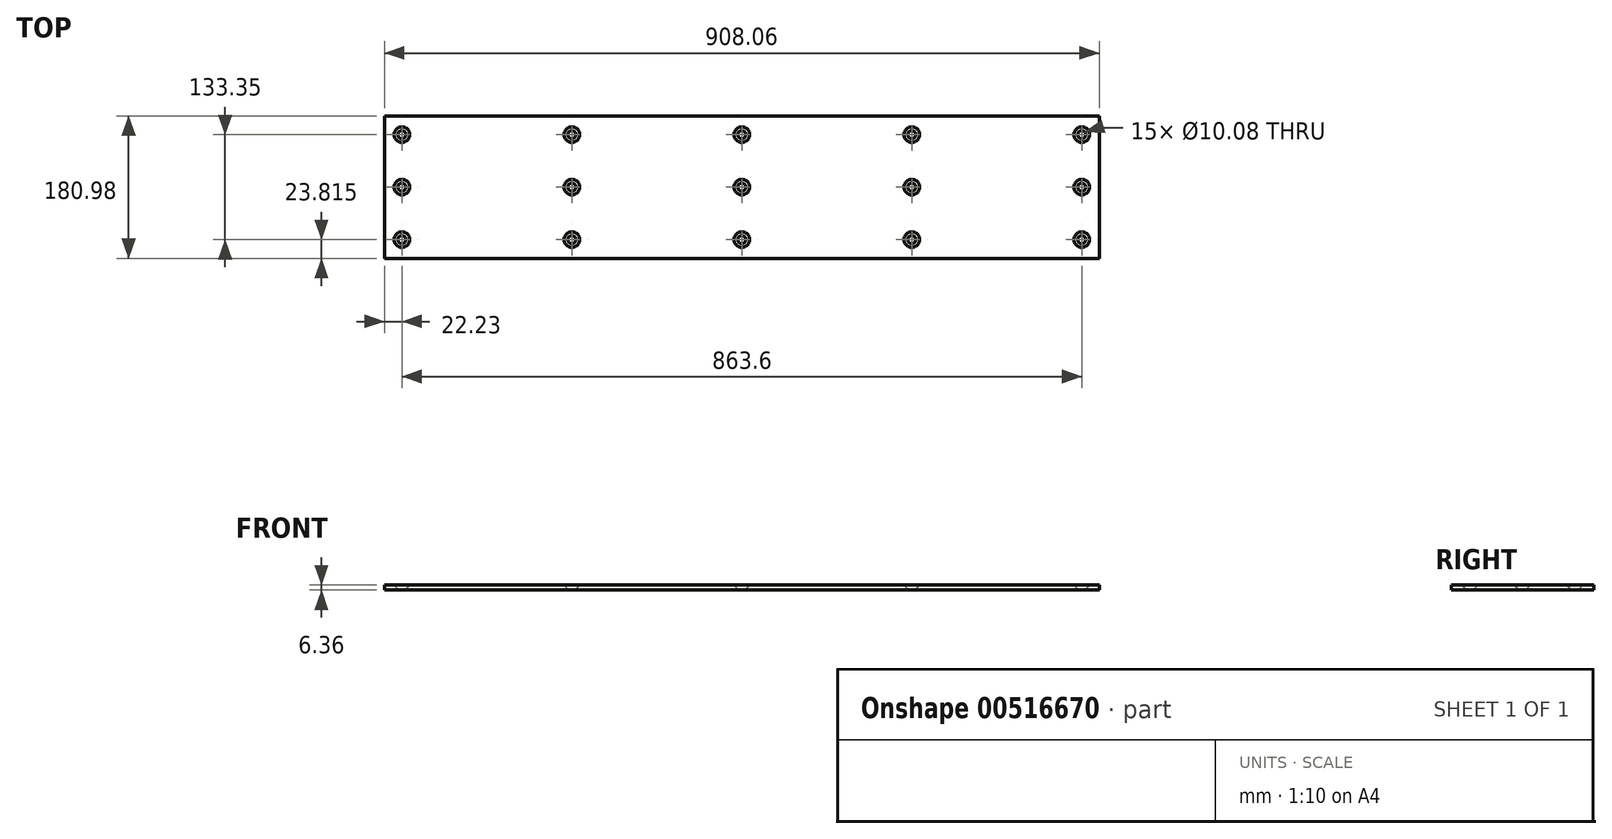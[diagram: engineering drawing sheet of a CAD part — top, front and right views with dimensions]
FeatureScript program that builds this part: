
annotation { "Feature Type Name" : "Feature", "Feature Type Description" : "" }
export const myFeature = defineFeature(function(context is Context, id is Id, definition is map)
    precondition{}
    {
        {
            var Q0;
            Q0=qCreatedBy(makeId("Top.planeOp"),FACE);
            var sketch = newSketch(context, id + "F0", { "sketchPlane" : qUnion([Q0])});
            skLineSegment(sketch, "E0.bottom", {"start": v(454.03, 90.49) * mm, "end": v(-454.03, 90.49) * mm});
            skLineSegment(sketch, "E0.top", {"start": v(454.03, -90.49) * mm, "end": v(-454.03, -90.49) * mm});
            skLineSegment(sketch, "E0.left", {"start": v(454.03, 90.49) * mm, "end": v(454.03, -90.49) * mm});
            skLineSegment(sketch, "E0.right", {"start": v(-454.03, 90.49) * mm, "end": v(-454.03, -90.49) * mm});
            skPoint(sketch, "E0.middle", {"position": v(0, 0) * mm});
            skSolve(sketch);
        }
        {
            var Q0;
            Q0 = qSketchRegion(id + "F0", true);
            extrude(context, id + "F1", {"entities" : qUnion([Q0]), "endBound" : BoundingType.SYMMETRIC, "depth" : 6.35 * mm, "offsetDistance" : 25.4 * mm});
        }
        {
            var Q0;
            Q0=makeQuery(id+"F1.opExtrude","CAP_FACE",FACE,{"disambiguationData":[OSD([sQuery(id+"F0.wireOp",EDGE,"E0.bottom"),sQuery(id+"F0.wireOp",EDGE,"E0.top"),sQuery(id+"F0.wireOp",EDGE,"E0.left"),sQuery(id+"F0.wireOp",EDGE,"E0.right")])],"isStart":false});
            var sketch = newSketch(context, id + "F2", { "sketchPlane" : qUnion([Q0])});
            skPoint(sketch, "E1", {"position": v(-431.8, 66.67) * mm});
            skPoint(sketch, "E2", {"position": v(-431.8, 0) * mm});
            skPoint(sketch, "E3", {"position": v(-431.8, -66.68) * mm});
            skPoint(sketch, "E4", {"position": v(-215.9, -66.68) * mm});
            skPoint(sketch, "E5", {"position": v(-215.9, 0) * mm});
            skPoint(sketch, "E6", {"position": v(-215.9, 66.67) * mm});
            skPoint(sketch, "E7", {"position": v(0, 66.67) * mm});
            skPoint(sketch, "E8", {"position": v(0, 0) * mm});
            skPoint(sketch, "E9", {"position": v(0, -66.68) * mm});
            skPoint(sketch, "E10", {"position": v(215.9, -66.68) * mm});
            skPoint(sketch, "E11", {"position": v(215.9, 0) * mm});
            skPoint(sketch, "E12", {"position": v(215.9, 66.67) * mm});
            skPoint(sketch, "E13", {"position": v(431.8, 66.67) * mm});
            skPoint(sketch, "E14", {"position": v(431.8, -66.68) * mm});
            skPoint(sketch, "E15", {"position": v(431.8, 0) * mm});
            skSolve(sketch);
        }
        {
            var Q0;
            Q0=sQuery(id+"F2.wireOp",VERTEX,"E1");
            var Q1;
            Q1=sQuery(id+"F2.wireOp",VERTEX,"E2");
            var Q2;
            Q2=sQuery(id+"F2.wireOp",VERTEX,"E3");
            var Q3;
            Q3=sQuery(id+"F2.wireOp",VERTEX,"E4");
            var Q4;
            Q4=sQuery(id+"F2.wireOp",VERTEX,"E5");
            var Q5;
            Q5=sQuery(id+"F2.wireOp",VERTEX,"E6");
            var Q6;
            Q6=sQuery(id+"F2.wireOp",VERTEX,"E7");
            var Q7;
            Q7=sQuery(id+"F2.wireOp",VERTEX,"E8");
            var Q8;
            Q8=sQuery(id+"F2.wireOp",VERTEX,"E9");
            var Q9;
            Q9=sQuery(id+"F2.wireOp",VERTEX,"E10");
            var Q10;
            Q10=sQuery(id+"F2.wireOp",VERTEX,"E11");
            var Q11;
            Q11=sQuery(id+"F2.wireOp",VERTEX,"E12");
            var Q12;
            Q12=sQuery(id+"F2.wireOp",VERTEX,"E13");
            var Q13;
            Q13=sQuery(id+"F2.wireOp",VERTEX,"E15");
            var Q14;
            Q14=sQuery(id+"F2.wireOp",VERTEX,"E14");
            var Q15;
            Q15=makeQuery(id+"F1.opExtrude","SWEPT_BODY",BODY,{"disambiguationData":[OSD([sQuery(id+"F0.wireOp",EDGE,"E0.bottom"),sQuery(id+"F0.wireOp",EDGE,"E0.top"),sQuery(id+"F0.wireOp",EDGE,"E0.left"),sQuery(id+"F0.wireOp",EDGE,"E0.right")])]});
            hole(context, id + "F3", {"style" : HoleStyle.C_SINK, "endStyle" : HoleEndStyle.THROUGH, "standardTappedOrClearance" : lookupTablePath({ "standard" : "ANSI", "fit" : "Normal (ASME)", "size" : "3/8", "type" : "Clearance" }), "standardBlindInLast" : lookupTablePath({ "fit" : "Free", "standard" : "ANSI", "size" : "3/8", "type" : "Clearance" }), "holeDiameter" : 10.08 * mm, "cSinkDiameter" : 19.84 * mm, "cSinkAngle" : 82 * degree, "isTappedThrough" : true, "tappedDepth" : 12.7 * mm, "tapClearance" : 3, "locations" : qUnion([Q0, Q1, Q2, Q3, Q4, Q5, Q6, Q7, Q8, Q9, Q10, Q11, Q12, Q13, Q14]), "scope" : qUnion([Q15])});
        }
    });
